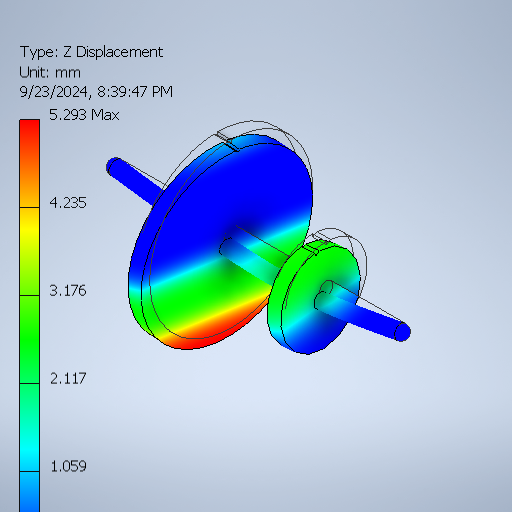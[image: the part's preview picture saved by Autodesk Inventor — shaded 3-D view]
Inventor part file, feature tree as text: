
AUTODESK INVENTOR PART (.ipt)
format: ipt  version: 2025 (Build 290162000, 162)  size: 373,760 bytes
history: native  units: mm
features: sketch x3, extrude x2, revolve x1
ambient origin geometry x8: Origin, YZ Plane, XZ Plane, XY Plane, X Axis, Y Axis, Z Axis, Center Point
bodies: Solid1 (feature_tree)
feature tree (6):
  revolve  "Revolution1"  [1 undecoded]
  extrude  "Extrusion1"  Depth=300.0mm
  extrude  "Extrusion2"  Depth=50.0mm
  sketch  "Sketch1"  dims[d0=400.0mm d1=350.0mm]
  sketch  "Sketch2"  dims[d2=300.0mm d3=300.0mm]
  sketch  "Sketch3"  dims[d4=25.0mm d5=50.0mm d6=1050.0mm d7=25.0mm d8=150.0mm d9=25.0mm d10=50.0mm d11=90.0deg d12=10.0mm d13=284.25mm d14=0.0mm d15=10.0mm d16=60.0deg d17=139.0mm d18=0.0mm]
note: 1 required parameter value undecoded (feature->parameter linkage not recoverable at this tier; creation-order binding heuristic only, values carry confidence <= 0.55)
